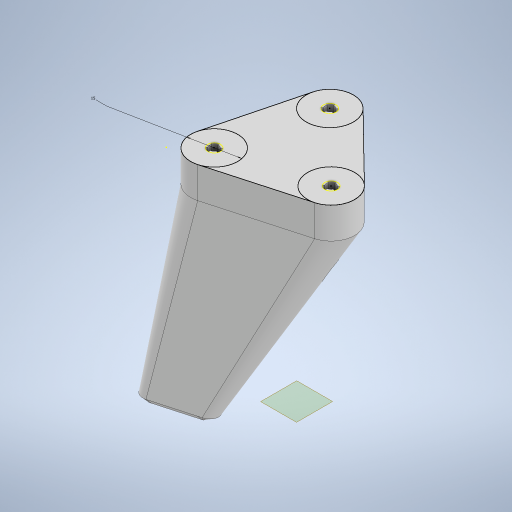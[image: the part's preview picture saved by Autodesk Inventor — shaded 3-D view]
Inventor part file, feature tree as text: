
AUTODESK INVENTOR PART (.ipt)
format: ipt  version: 2024.1 (Build 281209000, 209)  size: 535,552 bytes
history: native  units: mm
features: sketch x7, extrude x5, plane x3, chamfer x2, other x2, projected_geometry x2, loft x1
ambient origin geometry x8: Origin, YZ Plane, XZ Plane, XY Plane, X Axis, Y Axis, Z Axis, Center Point
bodies: Solid1 (feature_tree)
feature tree (22):
  extrude  "Extrusion1"  Depth=175.0mm
  extrude  "Extrusion3"  Depth=15.0mm
  chamfer  "Chamfer2"  Distance=30.0mm Angle=360.0deg
  extrude  "Extrusion4"  TaperAngle=0.0deg  [1 undecoded]
  sketch  "Sketch7"  dims[d16=7.5mm]
  plane  "Work Plane3"
  plane  "Work Plane4"
  loft  "Loft1"
  chamfer  "Chamfer4"  Distance=15.0mm
  extrude  "Extrusion5"  Depth=10.0mm TaperAngle=0.0deg
  plane  "Work Plane1"
  extrude  "Extrusion6"  Depth=2.0mm TaperAngle=45.0deg
  sketch  "Sketch1"  dims[d0=200.0mm d1=175.0mm]
  sketch  "Sketch3"  dims[d2=15.0mm d3=0.0mm d12=35.0mm]
  sketch  "Sketch4"  dims[d13=20.0mm]
  other  "leggie-boi"
  sketch  "Sketch5"  dims[d14=20.0mm]
  sketch  "Sketch6"  dims[d15=4.0mm]
  projected_geometry  "Projected Loop1"
  sketch  "Sketch9"  dims[d17=7.752551mm d18=30.0mm d20=360.0deg d22=0.0mm d23=0.0mm d24=2.8mm d25=2.0mm d26=45.0deg d27=15.0mm d31=10.0mm d32=0.0mm d36=2.5mm d37=2.0mm d38=45.0deg d39=0.0mm d40=0.0mm d46=60.0deg d47=60.0deg d48=8.0mm d49=2.8mm d50=60.0deg d51=60.0deg d52=60.0deg d53=60.0deg d54=60.25mm d55=50.5mm d56=0.0mm d62=60.0mm d65=7.0mm d66=2.7mm d67=2.7mm d68=3.0mm d69=0.0mm d70=90.0deg d71=0.0mm d72=90.0deg]
  projected_geometry  "Projected Loop2"
  other  "Edges1"
note: 1 required parameter value undecoded (feature->parameter linkage not recoverable at this tier; creation-order binding heuristic only, values carry confidence <= 0.55)
